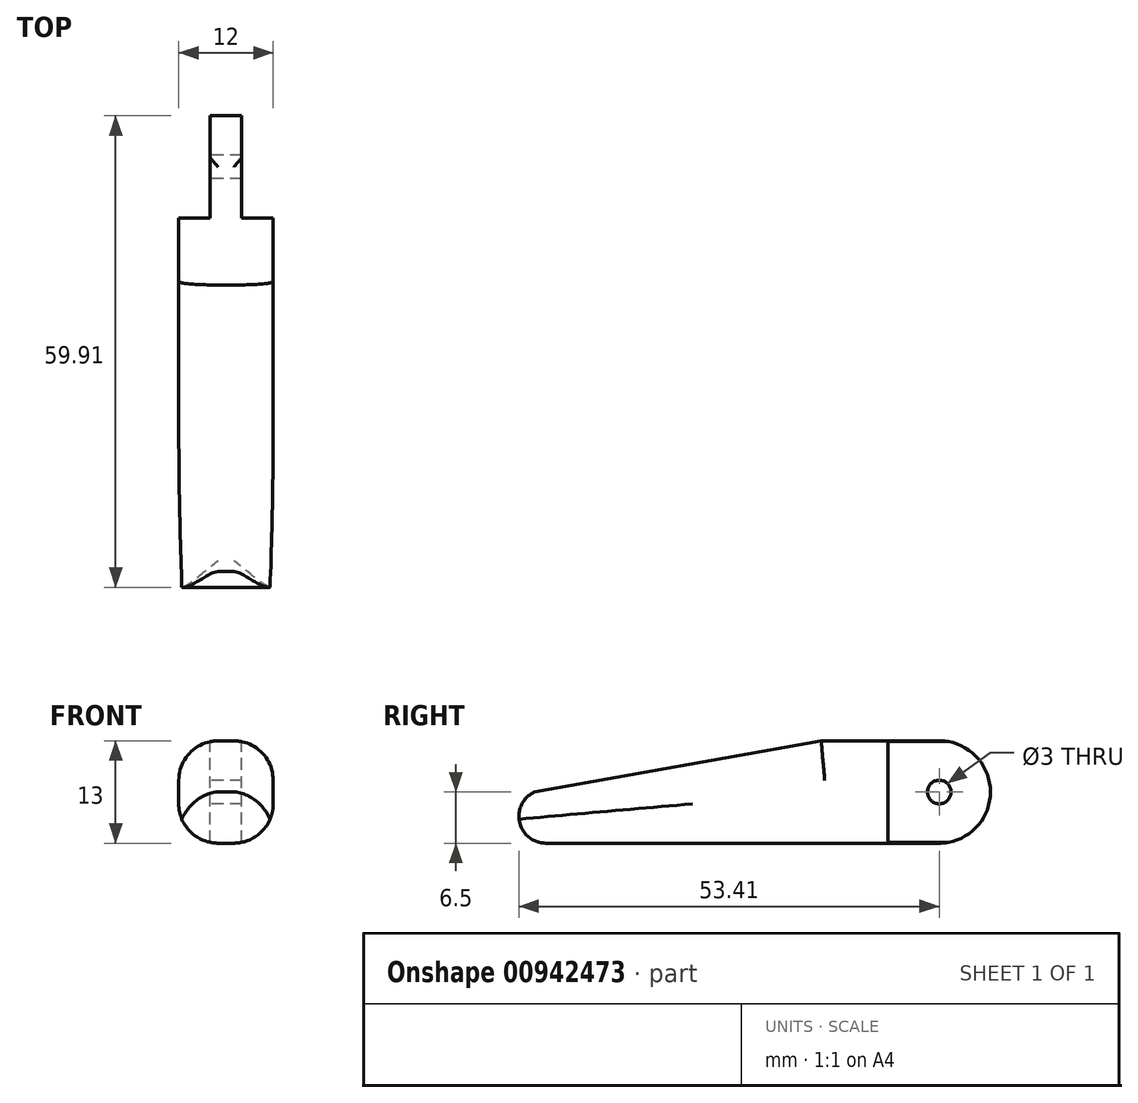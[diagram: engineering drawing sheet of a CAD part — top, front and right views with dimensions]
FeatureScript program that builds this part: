
annotation { "Feature Type Name" : "Feature", "Feature Type Description" : "" }
export const myFeature = defineFeature(function(context is Context, id is Id, definition is map)
    precondition{}
    {
        {
            var Q0;
            Q0=qCreatedBy(makeId("Right.planeOp"),FACE);
            var sketch = newSketch(context, id + "F0", { "sketchPlane" : qUnion([Q0])});
            skCircle(sketch, "E0", {"center": v(0, 0) * mm, "radius": 6.5 * mm});
            skCircle(sketch, "E1", {"center": v(0, 0) * mm, "radius": 1.5 * mm});
            skLineSegment(sketch, "E2", {"start": v(0, -6.5) * mm, "end": v(-50, -6.5) * mm});
            skLineSegment(sketch, "E3", {"start": v(0, 6.5) * mm, "end": v(-15, 6.5) * mm});
            skLineSegment(sketch, "E4", {"start": v(-15, 6.5) * mm, "end": v(-51.42, 0) * mm});
            skArc(sketch, "E5", {"start": v(-50, -6.5) * mm, "mid": v(-53.33, -3.82) * mm, "end": v(-51.42, 0) * mm});
            skLineSegment(sketch, "E6", {"start": v(-6.5, 0) * mm, "end": v(-6.5, 6.5) * mm});
            skLineSegment(sketch, "E7", {"start": v(-6.5, 0) * mm, "end": v(-6.5, -6.5) * mm});
            skSolve(sketch);
        }
        {
            var Q0;
            {var subQ1=sQuery(id+"F0.wireOp",EDGE,"E4");Q0=makeQuery(id+"F0.imprint","IMPRINT",FACE,{"disambiguationData":[TD([[makeQuery(id+"F0.imprint","IMPRINT",EDGE,{"derivedFrom":subQ1}),1.0]])]});}
            extrude(context, id + "F1", {"entities" : qUnion([Q0]), "depth" : 12 * mm, "offsetDistance" : 25 * mm});
        }
        {
            var Q0;
            Q0=makeQuery(id+"F0.imprint","IMPRINT",FACE,{"disambiguationData":[TD([[makeQuery(id+"F0.imprint","IMPRINT",EDGE,{"derivedFrom":sQuery(id+"F0.wireOp",EDGE,"E1")}),-1.0]])]});
            var Q1;
            {var subQ3=sQuery(id+"F0.wireOp",EDGE,"E6");Q1=makeQuery(id+"F0.imprint","IMPRINT",FACE,{"disambiguationData":[TD([[makeQuery(id+"F0.imprint","IMPRINT",EDGE,{"derivedFrom":subQ3}),-1.0]])]});}
            var Q2;
            {var subQ3=sQuery(id+"F0.wireOp",EDGE,"E7");Q2=makeQuery(id+"F0.imprint","IMPRINT",FACE,{"disambiguationData":[TD([[makeQuery(id+"F0.imprint","IMPRINT",EDGE,{"derivedFrom":subQ3}),1.0]])]});}
            extrude(context, id + "F2", {"entities" : qUnion([Q0, Q1, Q2]), "operationType" : NewBodyOperationType.ADD, "depth" : 8 * mm, "offsetDistance" : 25 * mm, "hasSecondDirection" : true, "secondDirectionOppositeDirection" : false, "secondDirectionDepth" : 4 * mm});
        }
        {
            var Q0;
            Q0=makeQuery(id+"F1.opExtrude","CAP_EDGE",EDGE,{"disambiguationData":[OSD([sQuery(id+"F0.wireOp",EDGE,"E3")])],"isStart":false});
            var Q1;
            Q1=makeQuery(id+"F1.opExtrude","CAP_EDGE",EDGE,{"disambiguationData":[OSD([sQuery(id+"F0.wireOp",EDGE,"E4")])],"isStart":false});
            var Q2;
            Q2=makeQuery(id+"F1.opExtrude","CAP_EDGE",EDGE,{"disambiguationData":[OSD([sQuery(id+"F0.wireOp",EDGE,"E3")])],"isStart":true});
            var Q3;
            Q3=makeQuery(id+"F1.opExtrude","CAP_EDGE",EDGE,{"disambiguationData":[OSD([sQuery(id+"F0.wireOp",EDGE,"E4")])],"isStart":true});
            var Q4;
            Q4=makeQuery(id+"F1.opExtrude","CAP_EDGE",EDGE,{"disambiguationData":[OSD([sQuery(id+"F0.wireOp",EDGE,"E2")])],"isStart":true});
            var Q5;
            Q5=makeQuery(id+"F1.opExtrude","CAP_EDGE",EDGE,{"disambiguationData":[OSD([sQuery(id+"F0.wireOp",EDGE,"E2")])],"isStart":false});
            fillet(context, id + "F3", {"entities" : qUnion([Q0, Q1, Q2, Q3, Q4, Q5]), "radius" : 5 * mm, "allowEdgeOverflow" : false});
        }
    });
